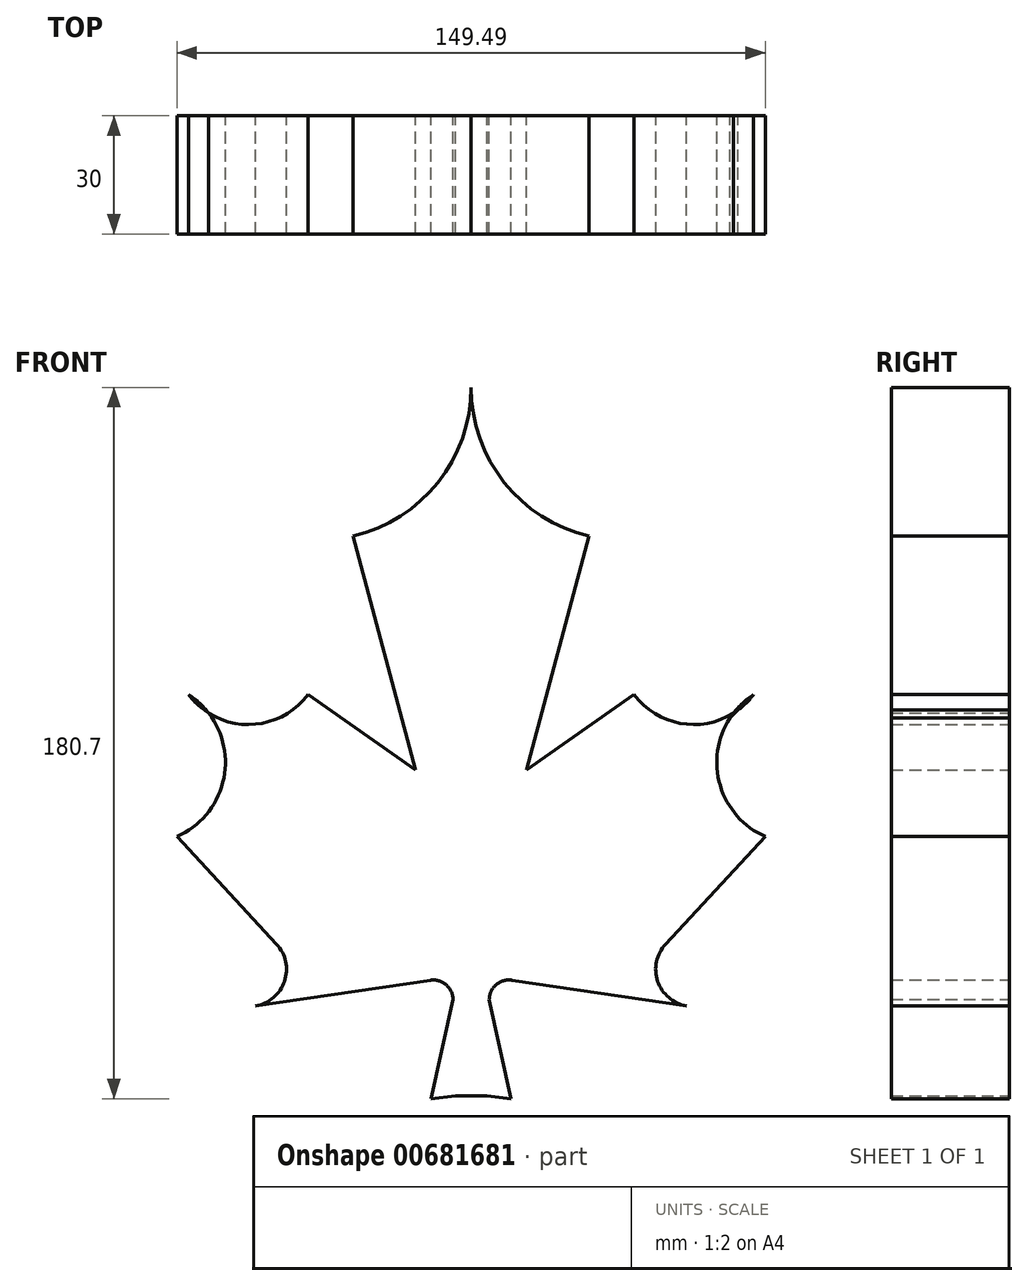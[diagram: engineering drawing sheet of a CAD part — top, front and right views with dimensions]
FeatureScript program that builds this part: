
annotation { "Feature Type Name" : "Feature", "Feature Type Description" : "" }
export const myFeature = defineFeature(function(context is Context, id is Id, definition is map)
    precondition{}
    {
        {
            var Q0;
            Q0=qCreatedBy(makeId("Front.planeOp"),FACE);
            var sketch = newSketch(context, id + "F0", { "sketchPlane" : qUnion([Q0])});
            skLineSegment(sketch, "E0.bottom", {"start": v(-11.74, -55.78) * mm, "end": v(-3.74, -55.77) * mm});
            skLineSegment(sketch, "E1", {"start": v(2.61, -26.38) * mm, "end": v(47, -32.9) * mm});
            skPoint(sketch, "E2.visualSharp", {"position": v(-11, -25.53) * mm});
            skPoint(sketch, "E3.visualSharp", {"position": v(-3, -25.56) * mm});
            skArc(sketch, "E3.filletArc", {"start": v(2.61, -26.38) * mm, "mid": v(-1.35, -27.5) * mm, "end": v(-3.14, -31.22) * mm});
            skLineSegment(sketch, "E4", {"start": v(-7.74, -55.78) * mm, "end": v(-7.74, -25.56) * mm});
            skLineSegment(sketch, "E5", {"start": v(58.02, 40.2) * mm, "end": v(64.05, 46.23) * mm});
            skLineSegment(sketch, "E6", {"start": v(6.35, 27.02) * mm, "end": v(22.27, 86.44) * mm});
            skPoint(sketch, "E7.end.orphan", {"position": v(-86.16, 10.1) * mm});
            skPoint(sketch, "E8.end.orphan", {"position": v(-61, -12.9) * mm});
            skPoint(sketch, "E9.end.orphan", {"position": v(-61, -32.9) * mm});
            skArc(sketch, "E10", {"start": v(64.05, 46.23) * mm, "mid": v(54.75, 27.29) * mm, "end": v(67, 10.1) * mm});
            skArc(sketch, "E11", {"start": v(33.67, 46.23) * mm, "mid": v(48.86, 38.58) * mm, "end": v(64.05, 46.23) * mm});
            skLineSegment(sketch, "E12", {"start": v(33.67, 46.23) * mm, "end": v(6.35, 27.02) * mm});
            skPoint(sketch, "E13.start.orphan", {"position": v(51.45, -12.9) * mm});
            skLineSegment(sketch, "E14", {"start": v(67, 10.1) * mm, "end": v(41.67, -17.23) * mm});
            skArc(sketch, "E15", {"start": v(41.67, -17.23) * mm, "mid": v(39.66, -26.65) * mm, "end": v(47, -32.9) * mm});
            skArc(sketch, "E16", {"start": v(-7.74, 124.22) * mm, "mid": v(0.67, 100.1) * mm, "end": v(22.27, 86.44) * mm});
            skPoint(sketch, "E17.orphan", {"position": v(-7.74, -25.56) * mm});
            skLineSegment(sketch, "E18", {"start": v(-3.74, -55.77) * mm, "end": v(2.46, -56.48) * mm});
            skLineSegment(sketch, "E19", {"start": v(2.46, -56.48) * mm, "end": v(-3.14, -31.22) * mm});
            skArc(sketch, "E20.MirrorCS", {"start": v(-7.74, 124.22) * mm, "mid": v(-16.16, 100.1) * mm, "end": v(-37.75, 86.44) * mm});
            skLineSegment(sketch, "E21.MirrorCS", {"start": v(-21.83, 27.02) * mm, "end": v(-37.75, 86.44) * mm});
            skLineSegment(sketch, "E22.MirrorCS", {"start": v(-49.16, 46.23) * mm, "end": v(-21.83, 27.02) * mm});
            skArc(sketch, "E23.MirrorCS", {"start": v(-49.16, 46.23) * mm, "mid": v(-64.34, 38.58) * mm, "end": v(-79.53, 46.23) * mm});
            skArc(sketch, "E24.MirrorCS", {"start": v(-79.53, 46.23) * mm, "mid": v(-70.24, 27.29) * mm, "end": v(-82.49, 10.1) * mm});
            skLineSegment(sketch, "E25.MirrorCS", {"start": v(-82.49, 10.1) * mm, "end": v(-57.15, -17.23) * mm});
            skArc(sketch, "E26.MirrorCS", {"start": v(-57.15, -17.23) * mm, "mid": v(-55.15, -26.65) * mm, "end": v(-62.49, -32.9) * mm});
            skLineSegment(sketch, "E27.MirrorCS", {"start": v(-18.1, -26.38) * mm, "end": v(-62.49, -32.9) * mm});
            skArc(sketch, "E28.MirrorCS", {"start": v(-18.1, -26.38) * mm, "mid": v(-14.13, -27.5) * mm, "end": v(-12.35, -31.22) * mm});
            skLineSegment(sketch, "E29.MirrorCS", {"start": v(-17.95, -56.48) * mm, "end": v(-12.35, -31.22) * mm});
            skLineSegment(sketch, "E30.MirrorCS", {"start": v(-11.74, -55.77) * mm, "end": v(-17.95, -56.48) * mm});
            skLineSegment(sketch, "E31.MirrorCS", {"start": v(-3.74, -55.78) * mm, "end": v(-11.74, -55.77) * mm});
            skSolve(sketch);
        }
        {
            var Q0;
            Q0 = qSketchRegion(id + "F0", true);
            extrude(context, id + "F1", {"entities" : qUnion([Q0]), "depth" : 30 * mm, "offsetDistance" : 25 * mm});
        }
    });
